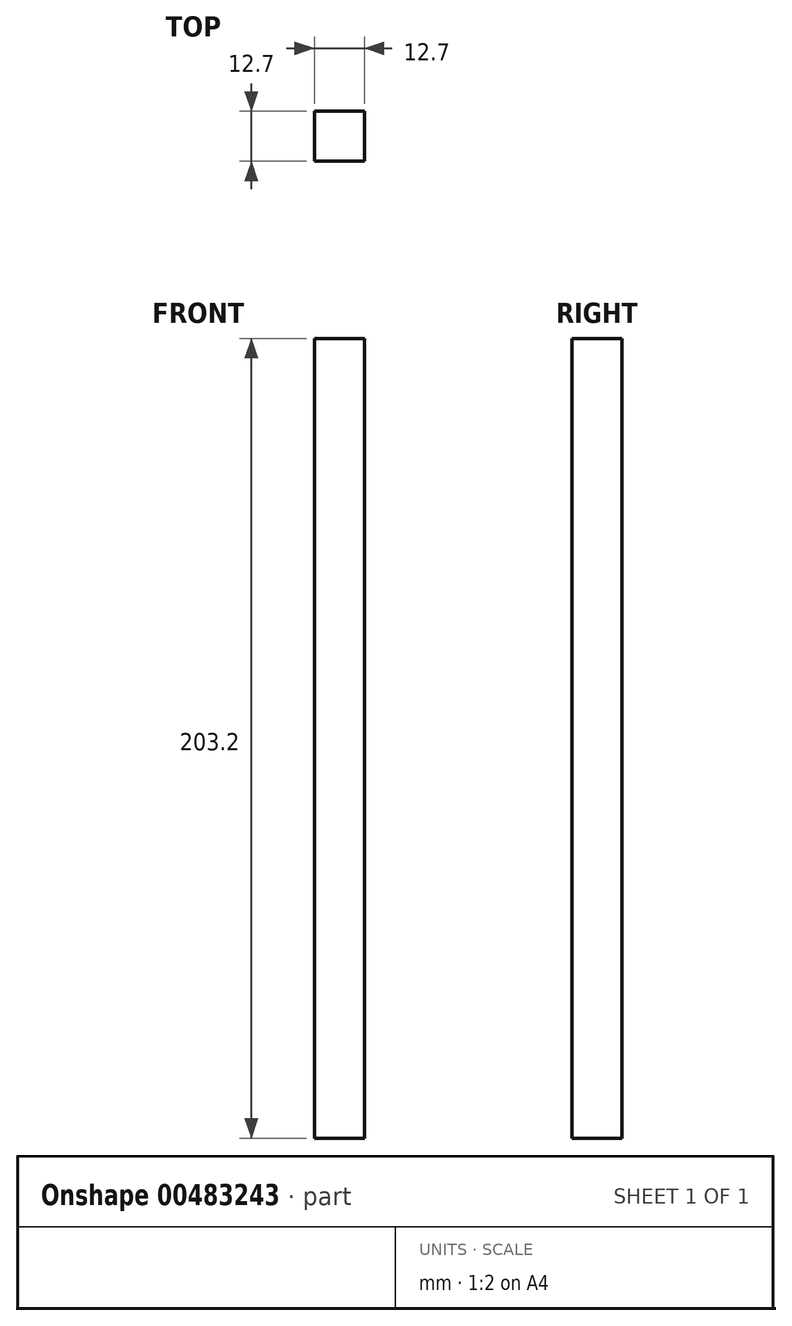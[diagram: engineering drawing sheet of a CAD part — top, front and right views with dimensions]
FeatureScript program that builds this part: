
annotation { "Feature Type Name" : "Feature", "Feature Type Description" : "" }
export const myFeature = defineFeature(function(context is Context, id is Id, definition is map)
    precondition{}
    {
        {
            var Q0;
            Q0=qCreatedBy(makeId("Top.planeOp"),FACE);
            var sketch = newSketch(context, id + "F0", { "sketchPlane" : qUnion([Q0])});
            skLineSegment(sketch, "E0.bottom", {"start": v(6.35, 6.35) * mm, "end": v(-6.35, 6.35) * mm});
            skLineSegment(sketch, "E0.top", {"start": v(6.35, -6.35) * mm, "end": v(-6.35, -6.35) * mm});
            skLineSegment(sketch, "E0.left", {"start": v(6.35, 6.35) * mm, "end": v(6.35, -6.35) * mm});
            skLineSegment(sketch, "E0.right", {"start": v(-6.35, 6.35) * mm, "end": v(-6.35, -6.35) * mm});
            skPoint(sketch, "E0.middle", {"position": v(0, 0) * mm});
            skSolve(sketch);
        }
        {
            var Q0;
            Q0 = qSketchRegion(id + "F0", true);
            extrude(context, id + "F1", {"entities" : qUnion([Q0]), "depth" : 203.2 * mm});
        }
    });
